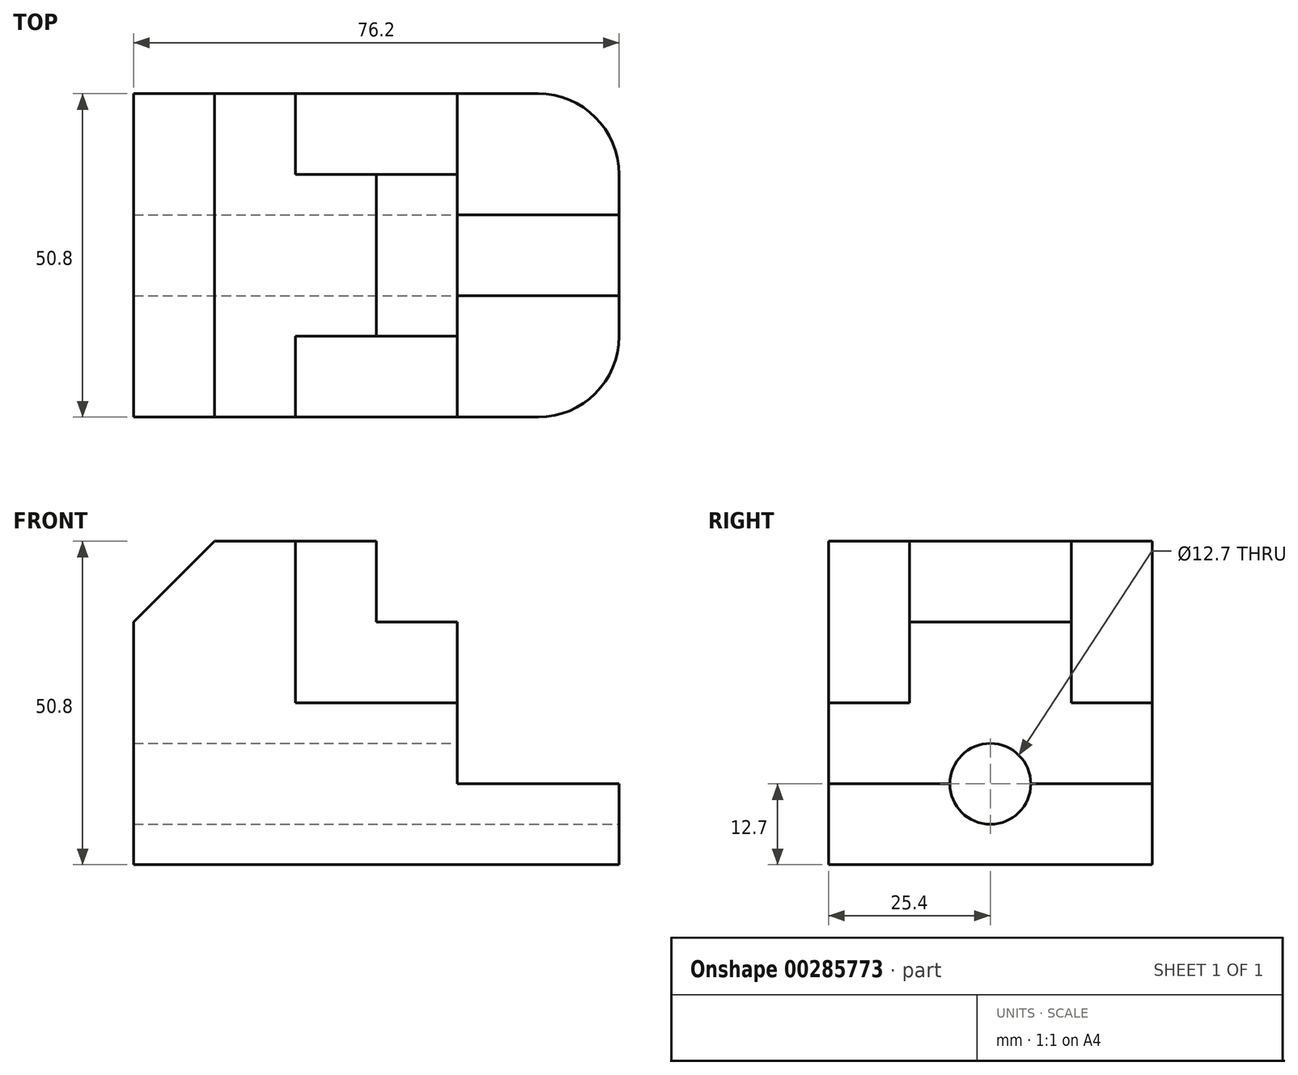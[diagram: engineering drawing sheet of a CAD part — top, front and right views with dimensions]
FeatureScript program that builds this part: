
annotation { "Feature Type Name" : "Feature", "Feature Type Description" : "" }
export const myFeature = defineFeature(function(context is Context, id is Id, definition is map)
    precondition{}
    {
        {
            var Q0;
            Q0=qCreatedBy(makeId("Right.planeOp"),FACE);
            var sketch = newSketch(context, id + "F0", { "sketchPlane" : qUnion([Q0])});
            skLineSegment(sketch, "E0", {"start": v(-25.4, 0) * mm, "end": v(25.4, 0) * mm});
            skLineSegment(sketch, "E1", {"start": v(25.4, 50.8) * mm, "end": v(-25.4, 50.8) * mm});
            skLineSegment(sketch, "E2", {"start": v(-25.4, 50.8) * mm, "end": v(-25.4, 0) * mm});
            skLineSegment(sketch, "E3", {"start": v(-25.4, 12.7) * mm, "end": v(25.4, 12.7) * mm});
            skLineSegment(sketch, "E4", {"start": v(-12.7, 50.8) * mm, "end": v(-12.7, 25.4) * mm});
            skLineSegment(sketch, "E5", {"start": v(-12.7, 25.4) * mm, "end": v(-25.4, 25.4) * mm});
            skLineSegment(sketch, "E6", {"start": v(12.7, 50.8) * mm, "end": v(12.7, 25.4) * mm});
            skLineSegment(sketch, "E7", {"start": v(12.7, 25.4) * mm, "end": v(25.4, 25.4) * mm});
            skLineSegment(sketch, "E8", {"start": v(25.4, 50.8) * mm, "end": v(25.4, 0) * mm});
            skSolve(sketch);
        }
        {
            var Q0;
            {var subQ0=sQuery(id+"F0.wireOp",EDGE,"E0");Q0=makeQuery(id+"F0.imprint","IMPRINT",FACE,{"disambiguationData":[TD([[makeQuery(id+"F0.imprint","IMPRINT",EDGE,{"derivedFrom":subQ0}),1.0]])]});}
            extrude(context, id + "F1", {"entities" : qUnion([Q0]), "depth" : 76.2 * mm});
        }
        {
            var Q0;
            Q0=makeQuery(id+"F1.opExtrude","CAP_FACE",FACE,{"disambiguationData":[OSD([sQuery(id+"F0.wireOp",EDGE,"E0"),sQuery(id+"F0.wireOp",EDGE,"E2"),sQuery(id+"F0.wireOp",EDGE,"E3"),sQuery(id+"F0.wireOp",EDGE,"E8")])],"isStart":false});
            var sketch = newSketch(context, id + "F2", { "sketchPlane" : qUnion([Q0])});
            skCircle(sketch, "E9", {"center": v(0, 12.7) * mm, "radius": 6.35 * mm});
            skSolve(sketch);
        }
        {
            var Q0;
            {var subQ0=sQuery(id+"F2.wireOp",EDGE,"E9");var subQ1=makeQuery(id+"F1.opExtrude","CAP_EDGE",EDGE,{"disambiguationData":[OSD([sQuery(id+"F0.wireOp",EDGE,"E3")])],"isStart":false});var subQ2=makeQuery(id+"F2.imprint","INTERSECT",VERTEX,{"disambiguationData":[OD(0.0)],"derivedFrom":[subQ1,subQ0]});Q0=makeQuery(id+"F2.imprint","IMPRINT",FACE,{"disambiguationData":[TD([[makeQuery(id+"F2.imprint","IMPRINT",EDGE,{"disambiguationData":[TD([[subQ2,1.0]])],"derivedFrom":subQ0}),1.0]])]});}
            var Q1;
            {var subQ0=sQuery(id+"F2.wireOp",EDGE,"E9");var subQ1=makeQuery(id+"F1.opExtrude","CAP_EDGE",EDGE,{"disambiguationData":[OSD([sQuery(id+"F0.wireOp",EDGE,"E3")])],"isStart":false});var subQ2=makeQuery(id+"F2.imprint","INTERSECT",VERTEX,{"disambiguationData":[OD(0.0)],"derivedFrom":[subQ1,subQ0]});Q1=makeQuery(id+"F2.imprint","IMPRINT",FACE,{"disambiguationData":[TD([[makeQuery(id+"F2.imprint","IMPRINT",EDGE,{"disambiguationData":[TD([[subQ2,-1.0]])],"derivedFrom":subQ0}),1.0]])]});}
            var Q2;
            Q2=sQuery(id+"F2.wireOp",EDGE,"E9");
            var Q3;
            Q3=makeQuery(id+"F1.opExtrude","CAP_FACE",FACE,{"disambiguationData":[OSD([sQuery(id+"F0.wireOp",EDGE,"E0"),sQuery(id+"F0.wireOp",EDGE,"E2"),sQuery(id+"F0.wireOp",EDGE,"E3"),sQuery(id+"F0.wireOp",EDGE,"E8")])],"isStart":true});
            extrude(context, id + "F3", {"entities" : qUnion([Q0, Q1]), "operationType" : NewBodyOperationType.REMOVE, "surfaceEntities" : qUnion([Q2]), "endBound" : BoundingType.UP_TO_SURFACE, "oppositeDirection" : true, "endBoundEntityFace" : qUnion([Q3]), "depth" : 25.4 * mm});
        }
        {
            var Q0;
            Q0=makeQuery(id+"F1.opExtrude","SWEPT_FACE",FACE,{"disambiguationData":[OSD([sQuery(id+"F0.wireOp",EDGE,"E2")])]});
            var sketch = newSketch(context, id + "F4", { "sketchPlane" : qUnion([Q0])});
            skSolve(sketch);
        }
        {
            var Q0;
            {var subQ1=sQuery(id+"F0.wireOp",EDGE,"E3");Q0=makeQuery(id+"F0.imprint","IMPRINT",FACE,{"disambiguationData":[TD([[makeQuery(id+"F0.imprint","IMPRINT",EDGE,{"derivedFrom":subQ1}),1.0]])]});}
            extrude(context, id + "F5", {"entities" : qUnion([Q0]), "operationType" : NewBodyOperationType.ADD, "depth" : 38.1 * mm});
        }
        {
            var Q0;
            {var subQ0=sQuery(id+"F0.wireOp",EDGE,"E2");Q0=makeQuery(id+"F4.imprint","IMPRINT",FACE,{"disambiguationData":[TD([[makeQuery(id+"F4.imprint","IMPRINT",EDGE,{"derivedFrom":makeQuery(id+"F1.opExtrude","CAP_EDGE",EDGE,{"disambiguationData":[OSD([subQ0])],"isStart":true})}),1.0]])]});}
            var sketch = newSketch(context, id + "F6", { "sketchPlane" : qUnion([Q0])});
            skLineSegment(sketch, "E10", {"start": v(0, 0) * mm, "end": v(25.4, 0) * mm});
            skLineSegment(sketch, "E11", {"start": v(25.4, 0) * mm, "end": v(25.4, 50.8) * mm});
            skLineSegment(sketch, "E12", {"start": v(25.4, 50.8) * mm, "end": v(12.7, 50.8) * mm});
            skLineSegment(sketch, "E13", {"start": v(12.7, 50.8) * mm, "end": v(0, 38.1) * mm});
            skLineSegment(sketch, "E14", {"start": v(0, 38.1) * mm, "end": v(0, 0) * mm});
            skSolve(sketch);
        }
        {
            var Q0;
            {var subQ0=sQuery(id+"F6.wireOp",EDGE,"E10");Q0=makeQuery(id+"F6.imprint","IMPRINT",FACE,{"disambiguationData":[TD([[makeQuery(id+"F6.imprint","IMPRINT",EDGE,{"derivedFrom":subQ0}),-1.0]])]});}
            var Q1;
            {var subQ4=sQuery(id+"F6.wireOp",EDGE,"E12");Q1=makeQuery(id+"F6.imprint","IMPRINT",FACE,{"disambiguationData":[TD([[makeQuery(id+"F6.imprint","IMPRINT",EDGE,{"derivedFrom":subQ4}),1.0]])]});}
            extrude(context, id + "F7", {"entities" : qUnion([Q0, Q1]), "operationType" : NewBodyOperationType.ADD, "oppositeDirection" : true, "depth" : 50.8 * mm});
        }
        {
            var Q0;
            {var subQ1=sQuery(id+"F0.wireOp",EDGE,"E4");Q0=makeQuery(id+"F7.boolean.opBoolean","SPLIT",FACE,{"disambiguationData":[TD([makeQuery(id+"F7.opExtrude","SWEPT_FACE",FACE,{"disambiguationData":[OSD([sQuery(id+"F6.wireOp",EDGE,"E13")])]})])],"derivedFrom":makeQuery(id+"F5.opExtrude","SWEPT_FACE",FACE,{"disambiguationData":[OSD([subQ1])]})});}
            extrude(context, id + "F8", {"entities" : qUnion([Q0]), "operationType" : NewBodyOperationType.REMOVE, "oppositeDirection" : true, "depth" : 45.97 * mm});
        }
        {
            var Q0;
            Q0=makeQuery(id+"F7.boolean.opBoolean","SPLIT",FACE,{"disambiguationData":[TD([makeQuery(id+"F3.boolean.opBoolean","COPY",FACE,{"derivedFrom":makeQuery(id+"F3.opExtrude","SWEPT_FACE",FACE,{"disambiguationData":[OSD([sQuery(id+"F2.wireOp",EDGE,"E9")])]})})])],"derivedFrom":makeQuery(id+"F7.opExtrude","SWEPT_FACE",FACE,{"disambiguationData":[OSD([sQuery(id+"F6.wireOp",EDGE,"E11")])]})});
            var Q1;
            {var subQ0=sQuery(id+"F2.wireOp",EDGE,"E9");var subQ1=makeQuery(id+"F1.opExtrude","CAP_EDGE",EDGE,{"disambiguationData":[OSD([sQuery(id+"F0.wireOp",EDGE,"E3")])],"isStart":false});var subQ2=makeQuery(id+"F2.imprint","INTERSECT",VERTEX,{"disambiguationData":[OD(0.0)],"derivedFrom":[subQ1,subQ0]});Q1=makeQuery(id+"F2.imprint","IMPRINT",FACE,{"disambiguationData":[TD([[makeQuery(id+"F2.imprint","IMPRINT",EDGE,{"disambiguationData":[TD([[subQ2,1.0]])],"derivedFrom":subQ0}),1.0]])]});}
            var Q2;
            {var subQ0=sQuery(id+"F2.wireOp",EDGE,"E9");var subQ1=makeQuery(id+"F1.opExtrude","CAP_EDGE",EDGE,{"disambiguationData":[OSD([sQuery(id+"F0.wireOp",EDGE,"E3")])],"isStart":false});var subQ2=makeQuery(id+"F2.imprint","INTERSECT",VERTEX,{"disambiguationData":[OD(0.0)],"derivedFrom":[subQ1,subQ0]});Q2=makeQuery(id+"F2.imprint","IMPRINT",FACE,{"disambiguationData":[TD([[makeQuery(id+"F2.imprint","IMPRINT",EDGE,{"disambiguationData":[TD([[subQ2,-1.0]])],"derivedFrom":subQ0}),1.0]])]});}
            var Q3;
            {var subQ0=sQuery(id+"F0.wireOp",EDGE,"E8");var subQ1=sQuery(id+"F0.wireOp",EDGE,"E3");var subQ2=sQuery(id+"F0.wireOp",EDGE,"E2");Q3=makeQuery(id+"F7.boolean.opBoolean","MERGE",FACE,{"derivedFrom":[makeQuery(id+"F5.boolean.opBoolean","MERGE",FACE,{"derivedFrom":[makeQuery(id+"F1.opExtrude","CAP_FACE",FACE,{"disambiguationData":[OSD([sQuery(id+"F0.wireOp",EDGE,"E0"),subQ2,subQ1,subQ0])],"isStart":true}),makeQuery(id+"F5.opExtrude","CAP_FACE",FACE,{"disambiguationData":[OSD([sQuery(id+"F0.wireOp",EDGE,"E1"),subQ2,subQ1,sQuery(id+"F0.wireOp",EDGE,"E4"),sQuery(id+"F0.wireOp",EDGE,"E5"),sQuery(id+"F0.wireOp",EDGE,"E6"),sQuery(id+"F0.wireOp",EDGE,"E7"),subQ0])],"isStart":true})]}),makeQuery(id+"F7.opExtrude","SWEPT_FACE",FACE,{"disambiguationData":[OSD([sQuery(id+"F6.wireOp",EDGE,"E14")])]})]});}
            extrude(context, id + "F9", {"entities" : qUnion([Q0, Q1, Q2]), "operationType" : NewBodyOperationType.REMOVE, "endBound" : BoundingType.UP_TO_SURFACE, "oppositeDirection" : true, "endBoundEntityFace" : qUnion([Q3]), "depth" : 25.4 * mm});
        }
        {
            var Q0;
            {var subQ0=sQuery(id+"F0.wireOp",EDGE,"E2");Q0=makeQuery(id+"F7.boolean.opBoolean","MERGE",FACE,{"derivedFrom":[makeQuery(id+"F5.boolean.opBoolean","MERGE",FACE,{"derivedFrom":[makeQuery(id+"F1.opExtrude","SWEPT_FACE",FACE,{"disambiguationData":[OSD([subQ0])]}),makeQuery(id+"F5.opExtrude","SWEPT_FACE",FACE,{"disambiguationData":[OSD([subQ0])]})]}),makeQuery(id+"F7.opExtrude","CAP_FACE",FACE,{"disambiguationData":[OSD([sQuery(id+"F6.wireOp",EDGE,"E10"),sQuery(id+"F6.wireOp",EDGE,"E11"),sQuery(id+"F6.wireOp",EDGE,"E12"),sQuery(id+"F6.wireOp",EDGE,"E13"),sQuery(id+"F6.wireOp",EDGE,"E14")])],"isStart":true})]});}
            var sketch = newSketch(context, id + "F10", { "sketchPlane" : qUnion([Q0])});
            skLineSegment(sketch, "E15", {"start": v(38.1, 25.4) * mm, "end": v(50.8, 25.4) * mm});
            skLineSegment(sketch, "E16", {"start": v(50.8, 25.4) * mm, "end": v(50.8, 12.7) * mm});
            skSolve(sketch);
        }
        {
            var Q0;
            Q0 = qSketchRegion(id + "F10", true);
            var Q1;
            Q1=makeQuery(id+"F10.imprint","IMPRINT",FACE,{"disambiguationData":[TD([[makeQuery(id+"F10.imprint","IMPRINT",EDGE,{"derivedFrom":sQuery(id+"F10.wireOp",EDGE,"E15")}),-1.0]])]});
            extrude(context, id + "F11", {"entities" : qUnion([Q0, Q1]), "operationType" : NewBodyOperationType.ADD, "oppositeDirection" : true, "depth" : 50.8 * mm});
        }
        {
            var Q0;
            {var subQ0=sQuery(id+"F2.wireOp",EDGE,"E9");var subQ1=makeQuery(id+"F1.opExtrude","CAP_EDGE",EDGE,{"disambiguationData":[OSD([sQuery(id+"F0.wireOp",EDGE,"E3")])],"isStart":false});var subQ2=makeQuery(id+"F2.imprint","INTERSECT",VERTEX,{"disambiguationData":[OD(0.0)],"derivedFrom":[subQ1,subQ0]});Q0=makeQuery(id+"F2.imprint","IMPRINT",FACE,{"disambiguationData":[TD([[makeQuery(id+"F2.imprint","IMPRINT",EDGE,{"disambiguationData":[TD([[subQ2,1.0]])],"derivedFrom":subQ0}),1.0]])]});}
            extrude(context, id + "F12", {"entities" : qUnion([Q0]), "operationType" : NewBodyOperationType.REMOVE, "oppositeDirection" : true, "depth" : 88.65 * mm});
        }
        {
            var Q0;
            Q0=makeQuery(id+"F11.boolean.opBoolean","MERGE",FACE,{"derivedFrom":[makeQuery(id+"F5.opExtrude","SWEPT_FACE",FACE,{"disambiguationData":[OSD([sQuery(id+"F0.wireOp",EDGE,"E5")])]}),makeQuery(id+"F5.opExtrude","SWEPT_FACE",FACE,{"disambiguationData":[OSD([sQuery(id+"F0.wireOp",EDGE,"E7")])]}),makeQuery(id+"F11.opExtrude","SWEPT_FACE",FACE,{"disambiguationData":[OSD([sQuery(id+"F10.wireOp",EDGE,"E15")])]})]});
            var sketch = newSketch(context, id + "F13", { "sketchPlane" : qUnion([Q0])});
            skLineSegment(sketch, "E17", {"start": v(38.1, -12.7) * mm, "end": v(50.8, -12.7) * mm});
            skLineSegment(sketch, "E18", {"start": v(38.1, 12.7) * mm, "end": v(50.8, 12.7) * mm});
            skSolve(sketch);
        }
        {
            var Q0;
            {var subQ0=sQuery(id+"F13.wireOp",EDGE,"E17");Q0=makeQuery(id+"F13.imprint","IMPRINT",FACE,{"disambiguationData":[TD([[makeQuery(id+"F13.imprint","IMPRINT",EDGE,{"derivedFrom":subQ0}),1.0]])]});}
            extrude(context, id + "F14", {"entities" : qUnion([Q0]), "operationType" : NewBodyOperationType.ADD, "depth" : 12.7 * mm});
        }
        {
            var Q0;
            Q0=makeQuery(id+"F1.opExtrude","SWEPT_FACE",FACE,{"disambiguationData":[OSD([sQuery(id+"F0.wireOp",EDGE,"E0")])]});
            var sketch = newSketch(context, id + "F15", { "sketchPlane" : qUnion([Q0])});
            skLineSegment(sketch, "E19", {"start": v(76.2, -12.7) * mm, "end": v(0, -12.7) * mm, "construction": true});
            skLineSegment(sketch, "E20", {"start": v(76.2, 12.7) * mm, "end": v(0, 12.7) * mm, "construction": true});
            skLineSegment(sketch, "E21", {"start": v(63.5, 25.4) * mm, "end": v(63.5, -25.4) * mm, "construction": true});
            skArc(sketch, "E22", {"start": v(63.5, -25.4) * mm, "mid": v(72.48, -21.68) * mm, "end": v(76.2, -12.7) * mm});
            skArc(sketch, "E23", {"start": v(76.2, 12.7) * mm, "mid": v(72.48, 21.68) * mm, "end": v(63.5, 25.4) * mm});
            skSolve(sketch);
        }
        {
            var Q0;
            {var subQ0=sQuery(id+"F15.wireOp",EDGE,"E23");Q0=makeQuery(id+"F15.imprint","IMPRINT",FACE,{"disambiguationData":[TD([[makeQuery(id+"F15.imprint","IMPRINT",EDGE,{"derivedFrom":subQ0}),-1.0]])]});}
            var Q1;
            {var subQ0=sQuery(id+"F15.wireOp",EDGE,"E22");Q1=makeQuery(id+"F15.imprint","IMPRINT",FACE,{"disambiguationData":[TD([[makeQuery(id+"F15.imprint","IMPRINT",EDGE,{"derivedFrom":subQ0}),-1.0]])]});}
            var Q2;
            {var subQ0=sQuery(id+"F0.wireOp",EDGE,"E8");var subQ1=sQuery(id+"F0.wireOp",EDGE,"E3");Q2=makeQuery(id+"F3.boolean.opBoolean","SPLIT",FACE,{"disambiguationData":[TD([makeQuery(id+"F1.opExtrude","SWEPT_FACE",FACE,{"disambiguationData":[OSD([subQ0])]})])],"derivedFrom":makeQuery(id+"F1.opExtrude","SWEPT_FACE",FACE,{"disambiguationData":[OSD([subQ1])]})});}
            extrude(context, id + "F16", {"entities" : qUnion([Q0, Q1]), "operationType" : NewBodyOperationType.REMOVE, "endBound" : BoundingType.UP_TO_SURFACE, "oppositeDirection" : true, "endBoundEntityFace" : qUnion([Q2]), "depth" : 25.4 * mm});
        }
    });
